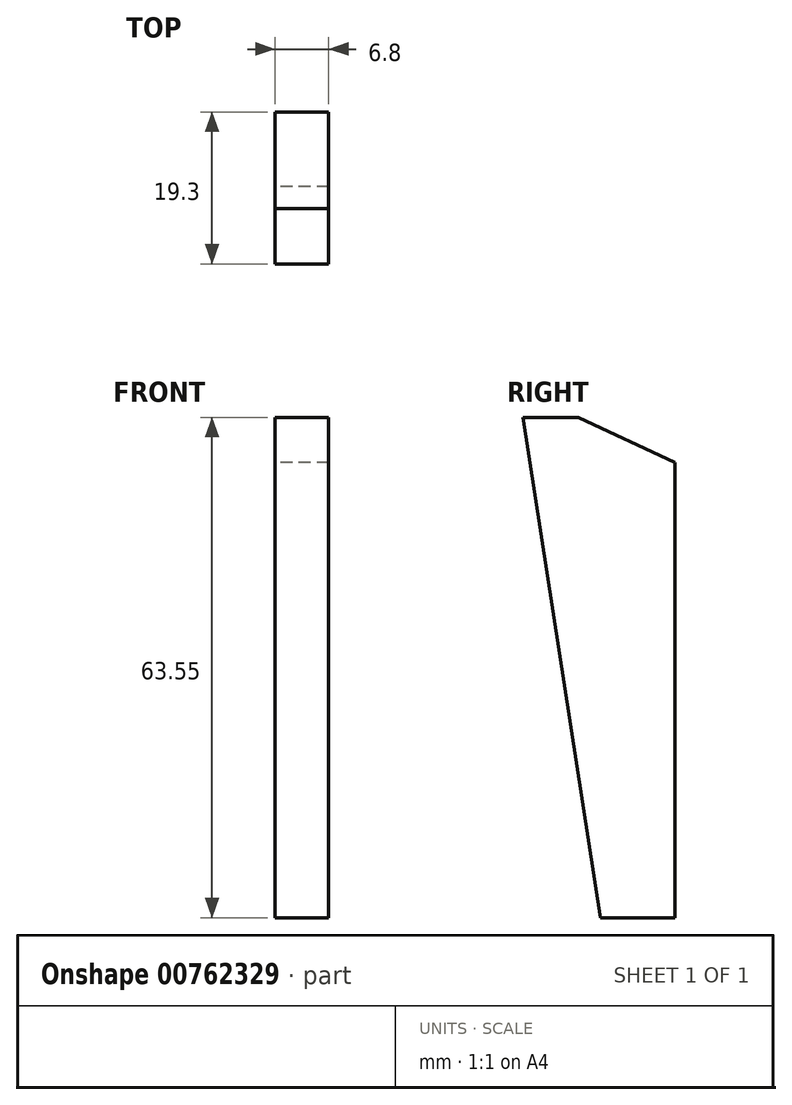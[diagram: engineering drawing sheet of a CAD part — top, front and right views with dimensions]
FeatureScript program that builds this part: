
annotation { "Feature Type Name" : "Feature", "Feature Type Description" : "" }
export const myFeature = defineFeature(function(context is Context, id is Id, definition is map)
    precondition{}
    {
        {
            var Q0;
            Q0=qCreatedBy(makeId("Right.planeOp"),FACE);
            var sketch = newSketch(context, id + "F0", { "sketchPlane" : qUnion([Q0])});
            skLineSegment(sketch, "E0", {"start": v(0, 0) * mm, "end": v(-9.5, 0) * mm});
            skLineSegment(sketch, "E1", {"start": v(-9.5, 0) * mm, "end": v(-19.3, 63.55) * mm});
            skLineSegment(sketch, "E2", {"start": v(0, 0) * mm, "end": v(0, 57.8) * mm});
            skLineSegment(sketch, "E3", {"start": v(-19.3, 63.55) * mm, "end": v(-12.3, 63.55) * mm});
            skLineSegment(sketch, "E4", {"start": v(-12.3, 63.55) * mm, "end": v(0, 57.8) * mm});
            skSolve(sketch);
        }
        {
            var Q0;
            Q0 = qSketchRegion(id + "F0", true);
            extrude(context, id + "F1", {"entities" : qUnion([Q0]), "endBound" : BoundingType.SYMMETRIC, "depth" : 6.8 * mm, "offsetDistance" : 25 * mm});
        }
    });
